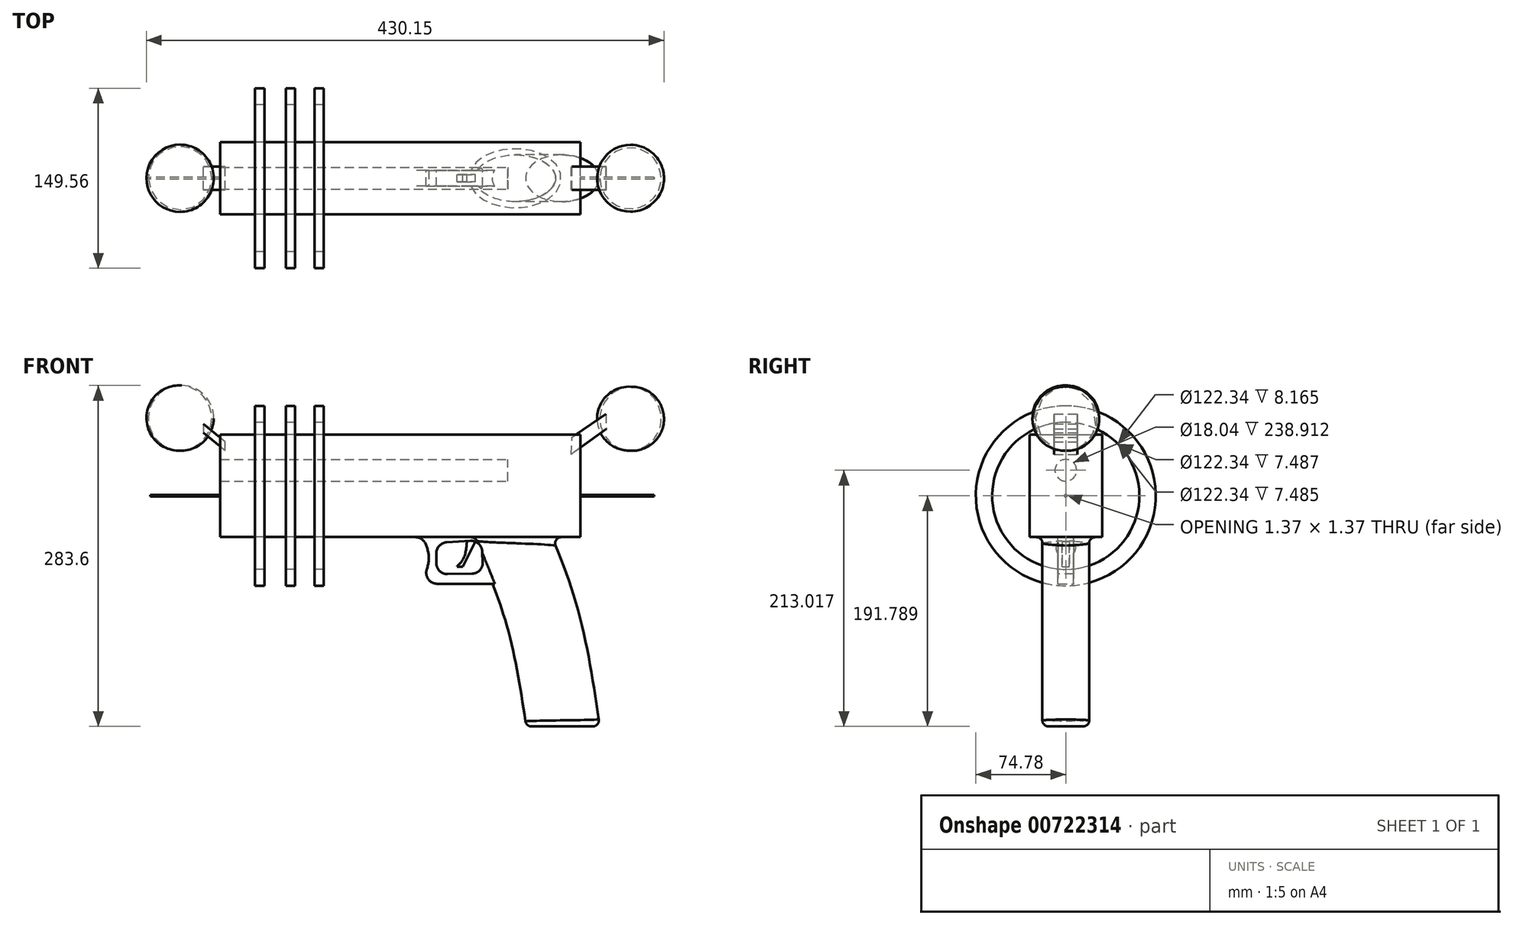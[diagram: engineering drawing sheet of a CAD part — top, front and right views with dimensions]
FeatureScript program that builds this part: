
annotation { "Feature Type Name" : "Feature", "Feature Type Description" : "" }
export const myFeature = defineFeature(function(context is Context, id is Id, definition is map)
    precondition{}
    {
        {
            var Q0;
            Q0=qCreatedBy(makeId("Top.planeOp"),FACE);
            var sketch = newSketch(context, id + "F0", { "sketchPlane" : qUnion([Q0])});
            skEllipse(sketch, "E0", {"center": v(45.97, 0) * mm, "majorRadius": 30.6 * mm, "minorRadius": 19.44 * mm, "majorAxis": v(1, 0)});
            skSolve(sketch);
        }
        {
            var Q0;
            Q0=qCreatedBy(makeId("Front.planeOp"),FACE);
            var sketch = newSketch(context, id + "F1", { "sketchPlane" : qUnion([Q0])});
            skFitSpline(sketch, "E1", {"points": [v(45.73, 0) * mm, v(28.39, 90.96) * mm, v(0, 166.43) * mm], "startDerivative": vector(-26.98, 180.89) * mm, "endDerivative": vector(-64.92, 151.63) * mm});
            skSolve(sketch);
        }
        {
            var Q0;
            Q0=makeQuery(id+"F0.imprint","IMPRINT",FACE,{"disambiguationData":[TD([[makeQuery(id+"F0.imprint","IMPRINT",EDGE,{"derivedFrom":sQuery(id+"F0.wireOp",EDGE,"E0")}),1.0]])]});
            var Q1;
            Q1=sQuery(id+"F1.wireOp",EDGE,"E1");
            sweep(context, id + "F2", {"profiles" : qUnion([Q0]), "path" : qUnion([Q1])});
        }
        {
            var Q0;
            Q0=qCreatedBy(makeId("Front.planeOp"),FACE);
            var sketch = newSketch(context, id + "F3", { "sketchPlane" : qUnion([Q0])});
            skLineSegment(sketch, "E2.bottom", {"start": v(60.54, 242.64) * mm, "end": v(-238.91, 242.64) * mm});
            skLineSegment(sketch, "E2.top", {"start": v(60.54, 157.45) * mm, "end": v(-238.91, 157.45) * mm});
            skLineSegment(sketch, "E2.left", {"start": v(60.54, 242.64) * mm, "end": v(60.54, 157.45) * mm});
            skLineSegment(sketch, "E2.right", {"start": v(-238.91, 242.64) * mm, "end": v(-238.91, 157.45) * mm});
            skSolve(sketch);
        }
        {
            var Q0;
            Q0 = qSketchRegion(id + "F3", true);
            extrude(context, id + "F4", {"entities" : qUnion([Q0]), "operationType" : NewBodyOperationType.ADD, "endBound" : BoundingType.SYMMETRIC, "depth" : 60.26 * mm, "offsetDistance" : 25.4 * mm});
        }
        {
            var Q0;
            Q0=qCreatedBy(makeId("Right.planeOp"),FACE);
            var sketch = newSketch(context, id + "F5", { "sketchPlane" : qUnion([Q0])});
            skCircle(sketch, "E3", {"center": v(0, 213.02) * mm, "radius": 9.02 * mm});
            skSolve(sketch);
        }
        {
            var Q0;
            Q0 = qSketchRegion(id + "F5", true);
            extrude(context, id + "F6", {"entities" : qUnion([Q0]), "operationType" : NewBodyOperationType.REMOVE, "oppositeDirection" : true, "depth" : 284.85 * mm, "offsetDistance" : 25.4 * mm});
        }
        {
            var Q0;
            Q0=qCreatedBy(makeId("Front.planeOp"),FACE);
            var sketch = newSketch(context, id + "F7", { "sketchPlane" : qUnion([Q0])});
            skFitSpline(sketch, "E4", {"points": [v(-71.24, 158.1) * mm, v(-65.62, 140.34) * mm, v(-72.06, 118.65) * mm], "startDerivative": vector(17.54, -36.38) * mm, "endDerivative": vector(-18.6, -42.42) * mm});
            skLineSegment(sketch, "E5", {"start": v(-72.06, 118.65) * mm, "end": v(-10.65, 118.65) * mm});
            skLineSegment(sketch, "E6", {"start": v(-10.65, 118.65) * mm, "end": v(-14.87, 165.6) * mm});
            skLineSegment(sketch, "E7", {"start": v(-14.87, 165.6) * mm, "end": v(-71.24, 158.1) * mm});
            skLineSegment(sketch, "E8", {"start": v(-59.36, 152.6) * mm, "end": v(-59.36, 126.52) * mm});
            skLineSegment(sketch, "E9", {"start": v(-59.36, 126.52) * mm, "end": v(-20.24, 127.3) * mm});
            skLineSegment(sketch, "E10", {"start": v(-20.24, 127.3) * mm, "end": v(-21.76, 154.89) * mm});
            skLineSegment(sketch, "E11", {"start": v(-21.76, 154.89) * mm, "end": v(-59.36, 152.6) * mm});
            skSolve(sketch);
        }
        {
            var Q0;
            Q0=makeQuery(id+"F7.imprint","IMPRINT",FACE,{"disambiguationData":[TD([[makeQuery(id+"F7.imprint","IMPRINT",EDGE,{"derivedFrom":sQuery(id+"F7.wireOp",EDGE,"E8")}),1.0]])]});
            extrude(context, id + "F8", {"entities" : qUnion([Q0]), "operationType" : NewBodyOperationType.REMOVE, "endBound" : BoundingType.SYMMETRIC, "oppositeDirection" : true, "depth" : 25.4 * mm, "offsetDistance" : 25.4 * mm});
        }
        {
            var Q0;
            Q0=makeQuery(id+"F7.imprint","IMPRINT",FACE,{"disambiguationData":[TD([[makeQuery(id+"F7.imprint","IMPRINT",EDGE,{"derivedFrom":sQuery(id+"F7.wireOp",EDGE,"E4")}),1.0]])]});
            extrude(context, id + "F9", {"entities" : qUnion([Q0]), "operationType" : NewBodyOperationType.ADD, "endBound" : BoundingType.SYMMETRIC, "depth" : 13.2 * mm, "offsetDistance" : 25.4 * mm});
        }
        {
            var Q0;
            Q0=makeQuery(id+"F9.opExtrude","SWEPT_EDGE",EDGE,{"disambiguationData":[OSD([sQuery(id+"F7.wireOp",EDGE,"E4"),sQuery(id+"F7.wireOp",EDGE,"E5")])]});
            var Q1;
            Q1=makeQuery(id+"F9.boolean.opBoolean","INTERSECT",EDGE,{"derivedFrom":[makeQuery(id+"F4.opExtrude","SWEPT_FACE",FACE,{"disambiguationData":[OSD([sQuery(id+"F3.wireOp",EDGE,"E2.top")])]}),makeQuery(id+"F9.opExtrude","SWEPT_FACE",FACE,{"disambiguationData":[OSD([sQuery(id+"F7.wireOp",EDGE,"E4")])]})]});
            var Q2;
            Q2=makeQuery(id+"F9.opExtrude","SWEPT_EDGE",EDGE,{"disambiguationData":[OSD([sQuery(id+"F7.wireOp",EDGE,"E8"),sQuery(id+"F7.wireOp",EDGE,"E11")])]});
            var Q3;
            Q3=makeQuery(id+"F9.opExtrude","SWEPT_EDGE",EDGE,{"disambiguationData":[OSD([sQuery(id+"F7.wireOp",EDGE,"E8"),sQuery(id+"F7.wireOp",EDGE,"E9")])]});
            var Q4;
            Q4=makeQuery(id+"F9.opExtrude","SWEPT_EDGE",EDGE,{"disambiguationData":[OSD([sQuery(id+"F7.wireOp",EDGE,"E9"),sQuery(id+"F7.wireOp",EDGE,"E10")])]});
            var Q5;
            Q5=makeQuery(id+"F8.boolean.opBoolean","COPY",EDGE,{"derivedFrom":makeQuery(id+"F8.opExtrude","SWEPT_EDGE",EDGE,{"disambiguationData":[OSD([sQuery(id+"F7.wireOp",EDGE,"E10"),sQuery(id+"F7.wireOp",EDGE,"E11")])]})});
            fillet(context, id + "F10", {"entities" : qUnion([Q0, Q1, Q2, Q3, Q4, Q5]), "radius" : 9.14 * mm, "tangentPropagation" : true, "allowEdgeOverflow" : false});
        }
        {
            var Q0;
            Q0=qCreatedBy(makeId("Front.planeOp"),FACE);
            var sketch = newSketch(context, id + "F11", { "sketchPlane" : qUnion([Q0])});
            skFitSpline(sketch, "E12", {"points": [v(-33.62, 156.43) * mm, v(-36.2, 141.02) * mm, v(-42.27, 132.72) * mm], "startDerivative": vector(-3.14, -26.24) * mm, "endDerivative": vector(-14.8, -16.18) * mm});
            skLineSegment(sketch, "E13", {"start": v(-42.27, 132.72) * mm, "end": v(-37.3, 132.72) * mm});
            skLineSegment(sketch, "E14", {"start": v(-37.3, 132.72) * mm, "end": v(-25.84, 156) * mm});
            skLineSegment(sketch, "E15", {"start": v(-25.84, 156) * mm, "end": v(-33.62, 156.43) * mm});
            skSolve(sketch);
        }
        {
            var Q0;
            Q0 = qSketchRegion(id + "F11", true);
            extrude(context, id + "F12", {"entities" : qUnion([Q0]), "operationType" : NewBodyOperationType.ADD, "endBound" : BoundingType.SYMMETRIC, "depth" : 5.87 * mm, "offsetDistance" : 25.4 * mm});
        }
        {
            var Q0;
            Q0=makeQuery(id+"F4.boolean.opBoolean","INTERSECT",EDGE,{"derivedFrom":[makeQuery(id+"F2.opSweep","SWEPT_FACE",FACE,{"disambiguationData":[OSD([sQuery(id+"F0.wireOp",EDGE,"E0"),sQuery(id+"F1.wireOp",EDGE,"E1")])]}),makeQuery(id+"F4.opExtrude","SWEPT_FACE",FACE,{"disambiguationData":[OSD([sQuery(id+"F3.wireOp",EDGE,"E2.top")])]})]});
            var Q1;
            Q1=makeQuery(id+"F2.opSweep","CAP_EDGE",EDGE,{"disambiguationData":[OSD([sQuery(id+"F0.wireOp",EDGE,"E0"),sQuery(id+"F1.wireOp",VERTEX,"E1.start")])],"isStart":true});
            fillet(context, id + "F13", {"entities" : qUnion([Q0, Q1]), "radius" : 5.08 * mm, "tangentPropagation" : true, "allowEdgeOverflow" : false});
        }
        {
            var Q0;
            Q0=qCreatedBy(makeId("Front.planeOp"),FACE);
            var sketch = newSketch(context, id + "F14", { "sketchPlane" : qUnion([Q0])});
            skArc(sketch, "E16", {"start": v(103.8, 282.42) * mm, "mid": v(76.72, 257.54) * mm, "end": v(100.37, 229.38) * mm});
            skArc(sketch, "E17", {"start": v(-272.73, 229.38) * mm, "mid": v(-244.38, 256.07) * mm, "end": v(-271.94, 283.58) * mm});
            skLineSegment(sketch, "E18", {"start": v(-271.89, 287.32) * mm, "end": v(-272.73, 229.38) * mm});
            skLineSegment(sketch, "E19", {"start": v(103.8, 282.42) * mm, "end": v(100.37, 229.38) * mm});
            skSolve(sketch);
        }
        {
            var Q0;
            {var subQ0=sQuery(id+"F14.wireOp",EDGE,"E17");Q0=makeQuery(id+"F14.imprint","IMPRINT",FACE,{"disambiguationData":[TD([[makeQuery(id+"F14.imprint","IMPRINT",EDGE,{"derivedFrom":subQ0}),1.0]])]});}
            var Q1;
            Q1=sQuery(id+"F14.wireOp",EDGE,"E18");
            revolve(context, id + "F15", {"surfaceOperationType" : NewSurfaceOperationType.NEW, "entities" : qUnion([Q0]), "axis" : qUnion([Q1]), "revolveType" : RevolveType.FULL});
        }
        {
            var Q0;
            Q0=makeQuery(id+"F14.imprint","IMPRINT",FACE,{"disambiguationData":[TD([[makeQuery(id+"F14.imprint","IMPRINT",EDGE,{"derivedFrom":sQuery(id+"F14.wireOp",EDGE,"E16")}),1.0]])]});
            var Q1;
            Q1=sQuery(id+"F14.wireOp",EDGE,"E19");
            revolve(context, id + "F16", {"surfaceOperationType" : NewSurfaceOperationType.NEW, "entities" : qUnion([Q0]), "axis" : qUnion([Q1]), "revolveType" : RevolveType.FULL});
        }
        {
            var Q0;
            Q0=qCreatedBy(makeId("Front.planeOp"),FACE);
            var sketch = newSketch(context, id + "F17", { "sketchPlane" : qUnion([Q0])});
            skLineSegment(sketch, "E20", {"start": v(-252.9, 244.41) * mm, "end": v(-234.92, 229.54) * mm});
            skLineSegment(sketch, "E21", {"start": v(-234.92, 229.54) * mm, "end": v(-234.92, 236.73) * mm});
            skLineSegment(sketch, "E22", {"start": v(-234.92, 236.73) * mm, "end": v(-252.9, 251.65) * mm});
            skLineSegment(sketch, "E23", {"start": v(-252.9, 251.65) * mm, "end": v(-252.9, 244.41) * mm});
            skLineSegment(sketch, "E24", {"start": v(53.37, 240.44) * mm, "end": v(81.65, 259.75) * mm});
            skLineSegment(sketch, "E25", {"start": v(81.65, 259.75) * mm, "end": v(81.9, 247.53) * mm});
            skLineSegment(sketch, "E26", {"start": v(81.9, 247.53) * mm, "end": v(52.85, 226.14) * mm});
            skLineSegment(sketch, "E27", {"start": v(52.85, 226.14) * mm, "end": v(53.37, 240.44) * mm});
            skSolve(sketch);
        }
        {
            var Q0;
            Q0=makeQuery(id+"F17.imprint","IMPRINT",FACE,{"disambiguationData":[TD([[makeQuery(id+"F17.imprint","IMPRINT",EDGE,{"derivedFrom":sQuery(id+"F17.wireOp",EDGE,"E20")}),1.0]])]});
            var Q1;
            Q1=makeQuery(id+"F17.imprint","IMPRINT",FACE,{"disambiguationData":[TD([[makeQuery(id+"F17.imprint","IMPRINT",EDGE,{"derivedFrom":sQuery(id+"F17.wireOp",EDGE,"E24")}),-1.0]])]});
            extrude(context, id + "F18", {"entities" : qUnion([Q0, Q1]), "endBound" : BoundingType.SYMMETRIC, "depth" : 19.35 * mm, "offsetDistance" : 25.4 * mm});
        }
        {
            var Q0;
            Q0=qCreatedBy(makeId("Front.planeOp"),FACE);
            var sketch = newSketch(context, id + "F19", { "sketchPlane" : qUnion([Q0])});
            skLineSegment(sketch, "E28.bottom", {"start": v(-210.19, 266.56) * mm, "end": v(-202.02, 266.56) * mm});
            skLineSegment(sketch, "E28.top", {"start": v(-210.19, 252.96) * mm, "end": v(-202.02, 252.96) * mm});
            skLineSegment(sketch, "E28.left", {"start": v(-210.19, 266.56) * mm, "end": v(-210.19, 252.96) * mm});
            skLineSegment(sketch, "E28.right", {"start": v(-202.02, 266.56) * mm, "end": v(-202.02, 252.96) * mm});
            skLineSegment(sketch, "E29.bottom", {"start": v(-184.4, 266.56) * mm, "end": v(-176.92, 266.56) * mm});
            skLineSegment(sketch, "E29.top", {"start": v(-184.4, 252.96) * mm, "end": v(-176.92, 252.96) * mm});
            skLineSegment(sketch, "E29.left", {"start": v(-184.4, 266.56) * mm, "end": v(-184.4, 252.96) * mm});
            skLineSegment(sketch, "E29.right", {"start": v(-176.92, 266.56) * mm, "end": v(-176.92, 252.96) * mm});
            skLineSegment(sketch, "E30.bottom", {"start": v(-160.58, 266.56) * mm, "end": v(-153.1, 266.56) * mm});
            skLineSegment(sketch, "E30.top", {"start": v(-160.58, 252.96) * mm, "end": v(-153.1, 252.96) * mm});
            skLineSegment(sketch, "E30.left", {"start": v(-160.58, 266.56) * mm, "end": v(-160.58, 252.96) * mm});
            skLineSegment(sketch, "E30.right", {"start": v(-153.1, 266.56) * mm, "end": v(-153.1, 252.96) * mm});
            skLineSegment(sketch, "E31.bottom", {"start": v(-297.21, 191.79) * mm, "end": v(121.64, 191.79) * mm});
            skLineSegment(sketch, "E31.top", {"start": v(-297.21, 192.47) * mm, "end": v(121.64, 192.47) * mm});
            skLineSegment(sketch, "E31.left", {"start": v(-297.21, 191.79) * mm, "end": v(-297.21, 192.47) * mm});
            skLineSegment(sketch, "E31.right", {"start": v(121.64, 191.79) * mm, "end": v(121.64, 192.47) * mm});
            skSolve(sketch);
        }
        {
            var Q0;
            Q0 = qSketchRegion(id + "F19", true);
            var Q1;
            Q1=sQuery(id+"F19.wireOp",EDGE,"E31.bottom");
            revolve(context, id + "F20", {"operationType" : NewBodyOperationType.ADD, "surfaceOperationType" : NewSurfaceOperationType.NEW, "entities" : qUnion([Q0]), "axis" : qUnion([Q1]), "revolveType" : RevolveType.FULL});
        }
    });
